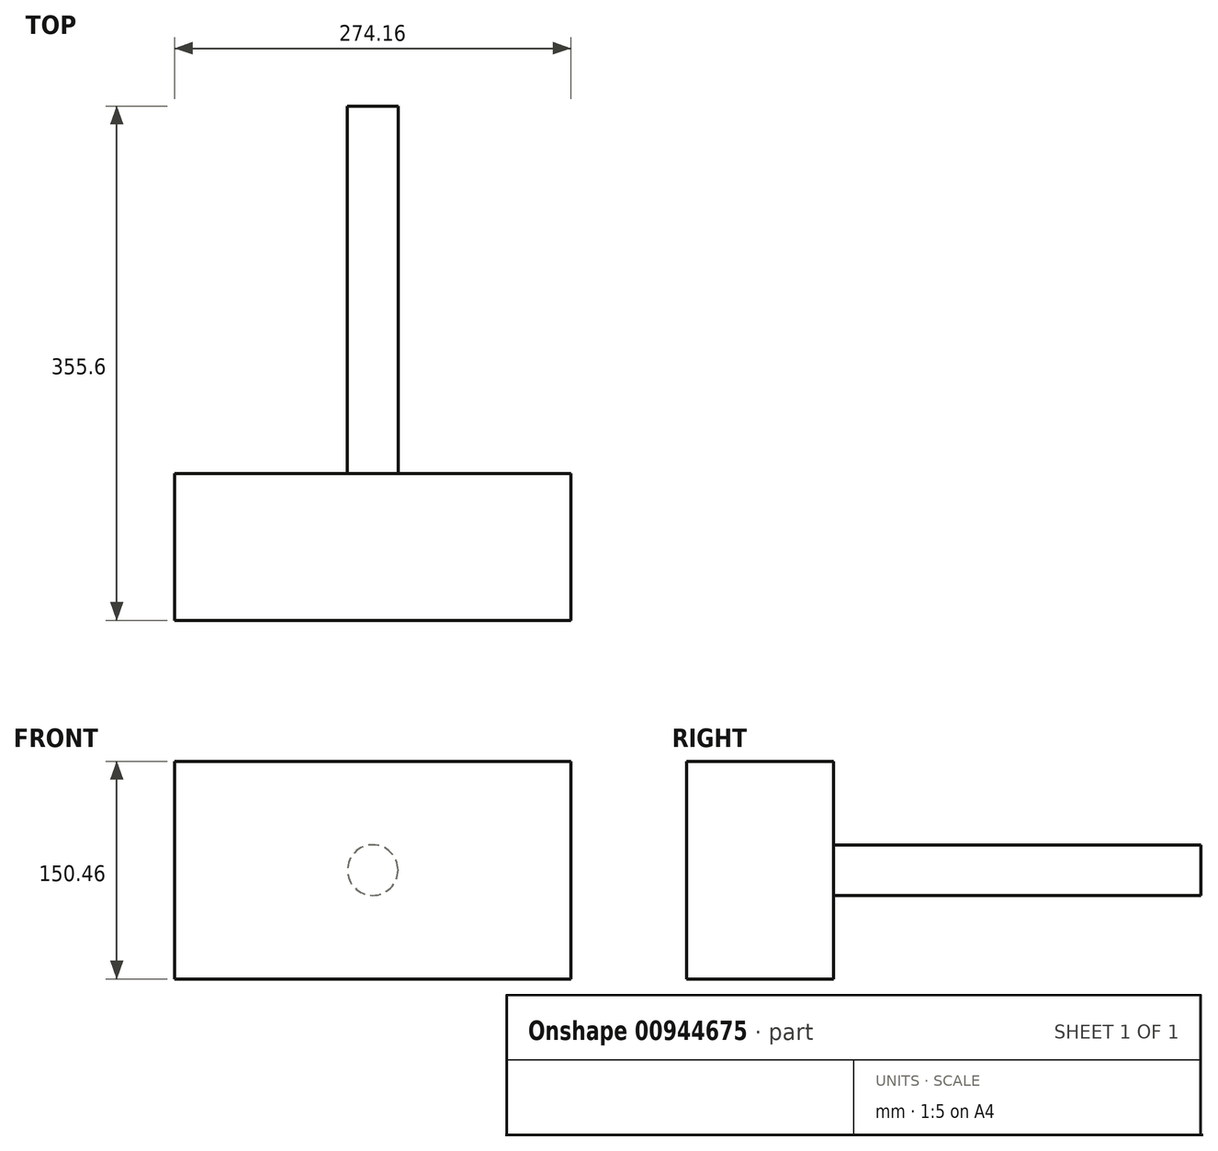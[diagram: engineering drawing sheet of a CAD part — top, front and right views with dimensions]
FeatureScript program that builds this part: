
annotation { "Feature Type Name" : "Feature", "Feature Type Description" : "" }
export const myFeature = defineFeature(function(context is Context, id is Id, definition is map)
    precondition{}
    {
        {
            var Q0;
            Q0=qCreatedBy(makeId("Front.planeOp"),FACE);
            var sketch = newSketch(context, id + "F0", { "sketchPlane" : qUnion([Q0])});
            skCircle(sketch, "E0", {"center": v(0, 0) * mm, "radius": 17.46 * mm});
            skSolve(sketch);
        }
        {
            var Q0;
            Q0=makeQuery(id+"F0.imprint","IMPRINT",FACE,{"disambiguationData":[TD([[makeQuery(id+"F0.imprint","IMPRINT",EDGE,{"derivedFrom":sQuery(id+"F0.wireOp",EDGE,"E0")}),1.0]])]});
            extrude(context, id + "F1", {"entities" : qUnion([Q0]), "depth" : 254 * mm, "offsetDistance" : 25.4 * mm});
        }
        {
            var Q0;
            Q0=makeQuery(id+"F1.opExtrude","CAP_FACE",FACE,{"disambiguationData":[OSD([sQuery(id+"F0.wireOp",EDGE,"E0")])],"isStart":false});
            var sketch = newSketch(context, id + "F2", { "sketchPlane" : qUnion([Q0])});
            skLineSegment(sketch, "E1.bottom", {"start": v(0, 0) * mm, "end": v(-137.08, 0) * mm});
            skLineSegment(sketch, "E1.top", {"start": v(0, 75.23) * mm, "end": v(-137.08, 75.23) * mm});
            skLineSegment(sketch, "E1.left", {"start": v(0, 0) * mm, "end": v(0, 75.23) * mm});
            skLineSegment(sketch, "E1.right", {"start": v(-137.08, 0) * mm, "end": v(-137.08, 75.23) * mm});
            skLineSegment(sketch, "E2.MirrorCS", {"start": v(0, 75.23) * mm, "end": v(137.08, 75.23) * mm});
            skLineSegment(sketch, "E3.MirrorCS", {"start": v(137.08, 0) * mm, "end": v(137.08, 75.23) * mm});
            skLineSegment(sketch, "E4.MirrorCS", {"start": v(0, 0) * mm, "end": v(137.08, 0) * mm});
            skLineSegment(sketch, "E5.MirrorCS", {"start": v(-137.08, 0) * mm, "end": v(-137.08, -75.23) * mm});
            skLineSegment(sketch, "E6.MirrorCS", {"start": v(0, -75.23) * mm, "end": v(-137.08, -75.23) * mm});
            skLineSegment(sketch, "E7.MirrorCS", {"start": v(0, -75.23) * mm, "end": v(137.08, -75.23) * mm});
            skLineSegment(sketch, "E8.MirrorCS", {"start": v(137.08, 0) * mm, "end": v(137.08, -75.23) * mm});
            skLineSegment(sketch, "E9.MirrorCS", {"start": v(0, 0) * mm, "end": v(0, -75.23) * mm});
            skSolve(sketch);
        }
        {
            var Q0;
            {var subQ1=sQuery(id+"F2.wireOp",EDGE,"E1.bottom");var subQ3=makeQuery(id+"F1.opExtrude","CAP_EDGE",EDGE,{"disambiguationData":[OSD([sQuery(id+"F0.wireOp",EDGE,"E0")])],"isStart":false});var subQ4=makeQuery(id+"F2.imprint","INTERSECT",VERTEX,{"derivedFrom":[subQ3,subQ1]});Q0=makeQuery(id+"F2.imprint","IMPRINT",FACE,{"disambiguationData":[TD([[makeQuery(id+"F2.imprint","IMPRINT",EDGE,{"disambiguationData":[TD([[subQ4,1.0]])],"derivedFrom":subQ3}),1.0]])]});}
            var Q1;
            {var subQ1=sQuery(id+"F2.wireOp",EDGE,"E1.bottom");var subQ3=makeQuery(id+"F1.opExtrude","CAP_EDGE",EDGE,{"disambiguationData":[OSD([sQuery(id+"F0.wireOp",EDGE,"E0")])],"isStart":false});var subQ4=makeQuery(id+"F2.imprint","INTERSECT",VERTEX,{"derivedFrom":[subQ3,subQ1]});Q1=makeQuery(id+"F2.imprint","IMPRINT",FACE,{"disambiguationData":[TD([[makeQuery(id+"F2.imprint","IMPRINT",EDGE,{"disambiguationData":[TD([[subQ4,-1.0]])],"derivedFrom":subQ3}),1.0]])]});}
            var Q2;
            {var subQ4=sQuery(id+"F2.wireOp",EDGE,"E5.MirrorCS");Q2=makeQuery(id+"F2.imprint","IMPRINT",FACE,{"disambiguationData":[TD([[makeQuery(id+"F2.imprint","IMPRINT",EDGE,{"derivedFrom":subQ4}),1.0]])]});}
            var Q3;
            {var subQ1=sQuery(id+"F2.wireOp",EDGE,"E1.left");var subQ3=makeQuery(id+"F1.opExtrude","CAP_EDGE",EDGE,{"disambiguationData":[OSD([sQuery(id+"F0.wireOp",EDGE,"E0")])],"isStart":false});var subQ4=makeQuery(id+"F2.imprint","INTERSECT",VERTEX,{"derivedFrom":[subQ3,subQ1]});Q3=makeQuery(id+"F2.imprint","IMPRINT",FACE,{"disambiguationData":[TD([[makeQuery(id+"F2.imprint","IMPRINT",EDGE,{"disambiguationData":[TD([[subQ4,1.0]])],"derivedFrom":subQ3}),1.0]])]});}
            var Q4;
            {var subQ6=sQuery(id+"F2.wireOp",EDGE,"E2.MirrorCS");Q4=makeQuery(id+"F2.imprint","IMPRINT",FACE,{"disambiguationData":[TD([[makeQuery(id+"F2.imprint","IMPRINT",EDGE,{"derivedFrom":subQ6}),-1.0]])]});}
            var Q5;
            {var subQ5=sQuery(id+"F2.wireOp",EDGE,"E7.MirrorCS");Q5=makeQuery(id+"F2.imprint","IMPRINT",FACE,{"disambiguationData":[TD([[makeQuery(id+"F2.imprint","IMPRINT",EDGE,{"derivedFrom":subQ5}),1.0]])]});}
            var Q6;
            {var subQ1=sQuery(id+"F2.wireOp",EDGE,"E4.MirrorCS");var subQ3=makeQuery(id+"F1.opExtrude","CAP_EDGE",EDGE,{"disambiguationData":[OSD([sQuery(id+"F0.wireOp",EDGE,"E0")])],"isStart":false});var subQ4=makeQuery(id+"F2.imprint","INTERSECT",VERTEX,{"derivedFrom":[subQ3,subQ1]});Q6=makeQuery(id+"F2.imprint","IMPRINT",FACE,{"disambiguationData":[TD([[makeQuery(id+"F2.imprint","IMPRINT",EDGE,{"disambiguationData":[TD([[subQ4,1.0]])],"derivedFrom":subQ3}),1.0]])]});}
            var Q7;
            {var subQ6=sQuery(id+"F2.wireOp",EDGE,"E1.top");Q7=makeQuery(id+"F2.imprint","IMPRINT",FACE,{"disambiguationData":[TD([[makeQuery(id+"F2.imprint","IMPRINT",EDGE,{"derivedFrom":subQ6}),1.0]])]});}
            extrude(context, id + "F3", {"entities" : qUnion([Q0, Q1, Q2, Q3, Q4, Q5, Q6, Q7]), "operationType" : NewBodyOperationType.ADD, "depth" : 76.2 * mm, "offsetDistance" : 25.4 * mm});
        }
        {
            var Q0;
            Q0=makeQuery(id+"F3.opExtrude","CAP_FACE",FACE,{"disambiguationData":[OSD([sQuery(id+"F2.wireOp",EDGE,"E1.top"),sQuery(id+"F2.wireOp",EDGE,"E1.right"),sQuery(id+"F2.wireOp",EDGE,"E2.MirrorCS"),sQuery(id+"F2.wireOp",EDGE,"E3.MirrorCS"),sQuery(id+"F2.wireOp",EDGE,"E5.MirrorCS"),sQuery(id+"F2.wireOp",EDGE,"E6.MirrorCS"),sQuery(id+"F2.wireOp",EDGE,"E7.MirrorCS"),sQuery(id+"F2.wireOp",EDGE,"E8.MirrorCS")])],"isStart":false});
            extrude(context, id + "F4", {"entities" : qUnion([Q0]), "operationType" : NewBodyOperationType.ADD, "depth" : 25.4 * mm, "offsetDistance" : 25.4 * mm});
        }
    });
